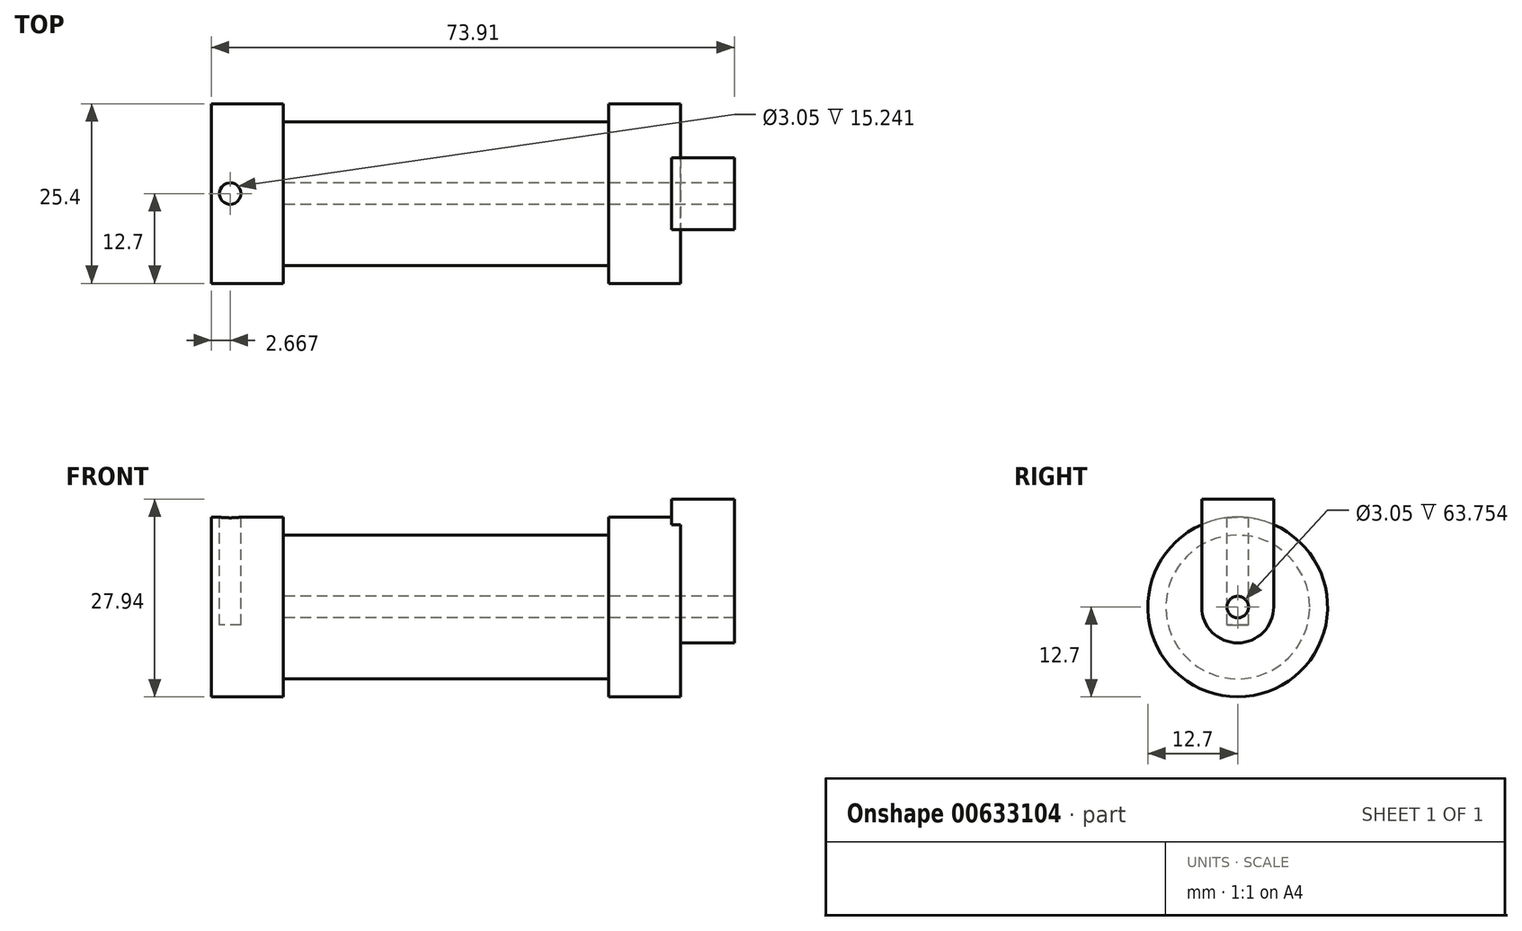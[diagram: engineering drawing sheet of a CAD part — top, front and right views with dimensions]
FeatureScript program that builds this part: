
annotation { "Feature Type Name" : "Feature", "Feature Type Description" : "" }
export const myFeature = defineFeature(function(context is Context, id is Id, definition is map)
    precondition{}
    {
        {
            var Q0;
            Q0=qCreatedBy(makeId("Front.planeOp"),FACE);
            var sketch = newSketch(context, id + "F0", { "sketchPlane" : qUnion([Q0])});
            skLineSegment(sketch, "E0", {"start": v(0, 0) * mm, "end": v(0, 12.7) * mm});
            skLineSegment(sketch, "E1", {"start": v(0, 12.7) * mm, "end": v(10.16, 12.7) * mm});
            skLineSegment(sketch, "E2", {"start": v(10.16, 12.7) * mm, "end": v(10.16, 10.16) * mm});
            skLineSegment(sketch, "E3", {"start": v(10.16, 10.16) * mm, "end": v(56.13, 10.16) * mm});
            skLineSegment(sketch, "E4", {"start": v(56.13, 10.16) * mm, "end": v(56.13, 12.7) * mm});
            skLineSegment(sketch, "E5", {"start": v(56.13, 12.7) * mm, "end": v(66.3, 12.7) * mm});
            skLineSegment(sketch, "E6", {"start": v(66.3, 12.7) * mm, "end": v(66.3, 0) * mm});
            skLineSegment(sketch, "E7", {"start": v(66.3, 0) * mm, "end": v(0, 0) * mm});
            skLineSegment(sketch, "E8", {"start": v(5.84, 15.24) * mm, "end": v(-0.5, 15.24) * mm});
            skLineSegment(sketch, "E9", {"start": v(-0.5, 15.24) * mm, "end": v(-10.88, 3.85) * mm});
            skLineSegment(sketch, "E10", {"start": v(0, 0) * mm, "end": v(-6.65, 0) * mm});
            skCircle(sketch, "E11", {"center": v(-6.65, 0) * mm, "radius": 5.72 * mm});
            skCircle(sketch, "E12", {"center": v(-6.65, 0) * mm, "radius": 3.18 * mm});
            skLineSegment(sketch, "E13", {"start": v(5.84, 15.24) * mm, "end": v(5.84, -9.4) * mm});
            skLineSegment(sketch, "E14", {"start": v(5.84, -9.4) * mm, "end": v(-8.18, -5.5) * mm});
            skSolve(sketch);
        }
        {
            var Q0;
            {var subQ0=sQuery(id+"F0.wireOp",EDGE,"E2");Q0=makeQuery(id+"F0.imprint","IMPRINT",FACE,{"disambiguationData":[TD([[makeQuery(id+"F0.imprint","IMPRINT",EDGE,{"derivedFrom":subQ0}),-1.0]])]});}
            var Q1;
            {var subQ0=sQuery(id+"F0.wireOp",EDGE,"E0");Q1=makeQuery(id+"F0.imprint","IMPRINT",FACE,{"disambiguationData":[TD([[makeQuery(id+"F0.imprint","IMPRINT",EDGE,{"derivedFrom":subQ0}),-1.0]])]});}
            var Q2;
            Q2=sQuery(id+"F0.wireOp",EDGE,"E7");
            revolve(context, id + "F1", {"entities" : qUnion([Q0, Q1]), "axis" : qUnion([Q2]), "revolveType" : RevolveType.FULL});
        }
        {
            var Q0;
            {var subQ1=sQuery(id+"F0.wireOp",EDGE,"E0");Q0=makeQuery(id+"F0.imprint","IMPRINT",FACE,{"disambiguationData":[TD([[makeQuery(id+"F0.imprint","IMPRINT",EDGE,{"derivedFrom":subQ1}),1.0]])]});}
            var Q1;
            {var subQ5=sQuery(id+"F0.wireOp",EDGE,"E12");Q1=makeQuery(id+"F0.imprint","IMPRINT",FACE,{"disambiguationData":[TD([[makeQuery(id+"F0.imprint","IMPRINT",EDGE,{"derivedFrom":subQ5}),-1.0]])]});}
            var Q2;
            {var subQ0=sQuery(id+"F0.wireOp",EDGE,"E14");Q2=makeQuery(id+"F0.imprint","IMPRINT",FACE,{"disambiguationData":[TD([[makeQuery(id+"F0.imprint","IMPRINT",EDGE,{"derivedFrom":subQ0}),-1.0]])]});}
            extrude(context, id + "F2", {"entities" : qUnion([Q0, Q1, Q2]), "endBound" : BoundingType.SYMMETRIC, "depth" : 6.35 * mm, "offsetDistance" : 25.4 * mm});
        }
        {
            var Q0;
            Q0=makeQuery(id+"F1.opRevolve","SWEPT_FACE",FACE,{"disambiguationData":[OSD([sQuery(id+"F0.wireOp",EDGE,"E6")])]});
            var sketch = newSketch(context, id + "F3", { "sketchPlane" : qUnion([Q0])});
            skCircle(sketch, "E15", {"center": v(0, 0) * mm, "radius": 1.52 * mm});
            skCircle(sketch, "E16", {"center": v(0, 0) * mm, "radius": 5.08 * mm});
            skLineSegment(sketch, "E17", {"start": v(-8, 0) * mm, "end": v(9.92, 0) * mm, "construction": true});
            skLineSegment(sketch, "E18", {"start": v(5.08, 0) * mm, "end": v(5.08, 15.24) * mm});
            skLineSegment(sketch, "E19", {"start": v(-5.08, 0) * mm, "end": v(-5.08, 15.24) * mm});
            skLineSegment(sketch, "E20", {"start": v(-5.08, 15.24) * mm, "end": v(5.08, 15.24) * mm});
            skSolve(sketch);
        }
        {
            var Q0;
            {var subQ0=sQuery(id+"F3.wireOp",EDGE,"E20");Q0=makeQuery(id+"F3.imprint","IMPRINT",FACE,{"disambiguationData":[TD([[makeQuery(id+"F3.imprint","IMPRINT",EDGE,{"derivedFrom":subQ0}),-1.0]])]});}
            var Q1;
            {var subQ0=sQuery(id+"F3.wireOp",EDGE,"E18");var subQ1=sQuery(id+"F3.wireOp",EDGE,"E16");var subQ2=makeQuery(id+"F3.imprint","INTERSECT",VERTEX,{"derivedFrom":[subQ1,subQ0]});Q1=makeQuery(id+"F3.imprint","IMPRINT",FACE,{"disambiguationData":[TD([[makeQuery(id+"F3.imprint","IMPRINT",EDGE,{"disambiguationData":[TD([[subQ2,-1.0]])],"derivedFrom":subQ1}),-1.0]])]});}
            var Q2;
            Q2=makeQuery(id+"F3.imprint","IMPRINT",FACE,{"disambiguationData":[TD([[makeQuery(id+"F3.imprint","IMPRINT",EDGE,{"derivedFrom":sQuery(id+"F3.wireOp",EDGE,"E15")}),-1.0]])]});
            extrude(context, id + "F4", {"entities" : qUnion([Q0, Q1, Q2]), "operationType" : NewBodyOperationType.ADD, "depth" : 7.62 * mm, "offsetDistance" : 25.4 * mm, "hasSecondDirection" : true, "secondDirectionOppositeDirection" : true, "secondDirectionDepth" : 1.27 * mm});
        }
        {
            var Q0;
            Q0=makeQuery(id+"F4.boolean.opBoolean","SPLIT",FACE,{"disambiguationData":[TD([makeQuery(id+"F4.opExtrude","SWEPT_FACE",FACE,{"disambiguationData":[OSD([sQuery(id+"F3.wireOp",EDGE,"E15")])]})])],"derivedFrom":makeQuery(id+"F1.opRevolve","SWEPT_FACE",FACE,{"disambiguationData":[OSD([sQuery(id+"F0.wireOp",EDGE,"E6")])]})});
            var Q1;
            Q1=makeQuery(id+"F1.opRevolve","SWEPT_FACE",FACE,{"disambiguationData":[OSD([sQuery(id+"F0.wireOp",EDGE,"E2")])]});
            extrude(context, id + "F5", {"entities" : qUnion([Q0]), "operationType" : NewBodyOperationType.REMOVE, "endBound" : BoundingType.UP_TO_SURFACE, "oppositeDirection" : true, "depth" : 25.4 * mm, "endBoundEntityFace" : qUnion([Q1]), "offsetDistance" : 25.4 * mm});
        }
        {
            var Q0;
            Q0=makeQuery(id+"F2.opExtrude","SWEPT_FACE",FACE,{"disambiguationData":[OSD([sQuery(id+"F0.wireOp",EDGE,"E8")])]});
            var sketch = newSketch(context, id + "F6", { "sketchPlane" : qUnion([Q0])});
            skCircle(sketch, "E21", {"center": v(2.67, 0) * mm, "radius": 1.52 * mm});
            skSolve(sketch);
        }
        {
            var Q0;
            Q0=makeQuery(id+"F6.imprint","IMPRINT",FACE,{"disambiguationData":[TD([[makeQuery(id+"F6.imprint","IMPRINT",EDGE,{"derivedFrom":sQuery(id+"F6.wireOp",EDGE,"E21")}),1.0]])]});
            var Q1;
            Q1=sQuery(id+"F6.wireOp",EDGE,"E21");
            extrude(context, id + "F7", {"entities" : qUnion([Q0]), "operationType" : NewBodyOperationType.REMOVE, "surfaceEntities" : qUnion([Q1]), "oppositeDirection" : true, "depth" : 17.78 * mm, "offsetDistance" : 25.4 * mm});
        }
        {
            var Q0;
            Q0=makeQuery(id+"F2.opExtrude","SWEPT_BODY",BODY,{"disambiguationData":[OSD([sQuery(id+"F0.wireOp",EDGE,"E0"),sQuery(id+"F0.wireOp",EDGE,"E1"),sQuery(id+"F0.wireOp",EDGE,"E7"),sQuery(id+"F0.wireOp",EDGE,"E8"),sQuery(id+"F0.wireOp",EDGE,"E9"),sQuery(id+"F0.wireOp",EDGE,"E11"),sQuery(id+"F0.wireOp",EDGE,"E12"),sQuery(id+"F0.wireOp",EDGE,"E13"),sQuery(id+"F0.wireOp",EDGE,"E14")])]});
            deleteBodies(context, id + "F8", {"entities" : qUnion([Q0])});
        }
    });
